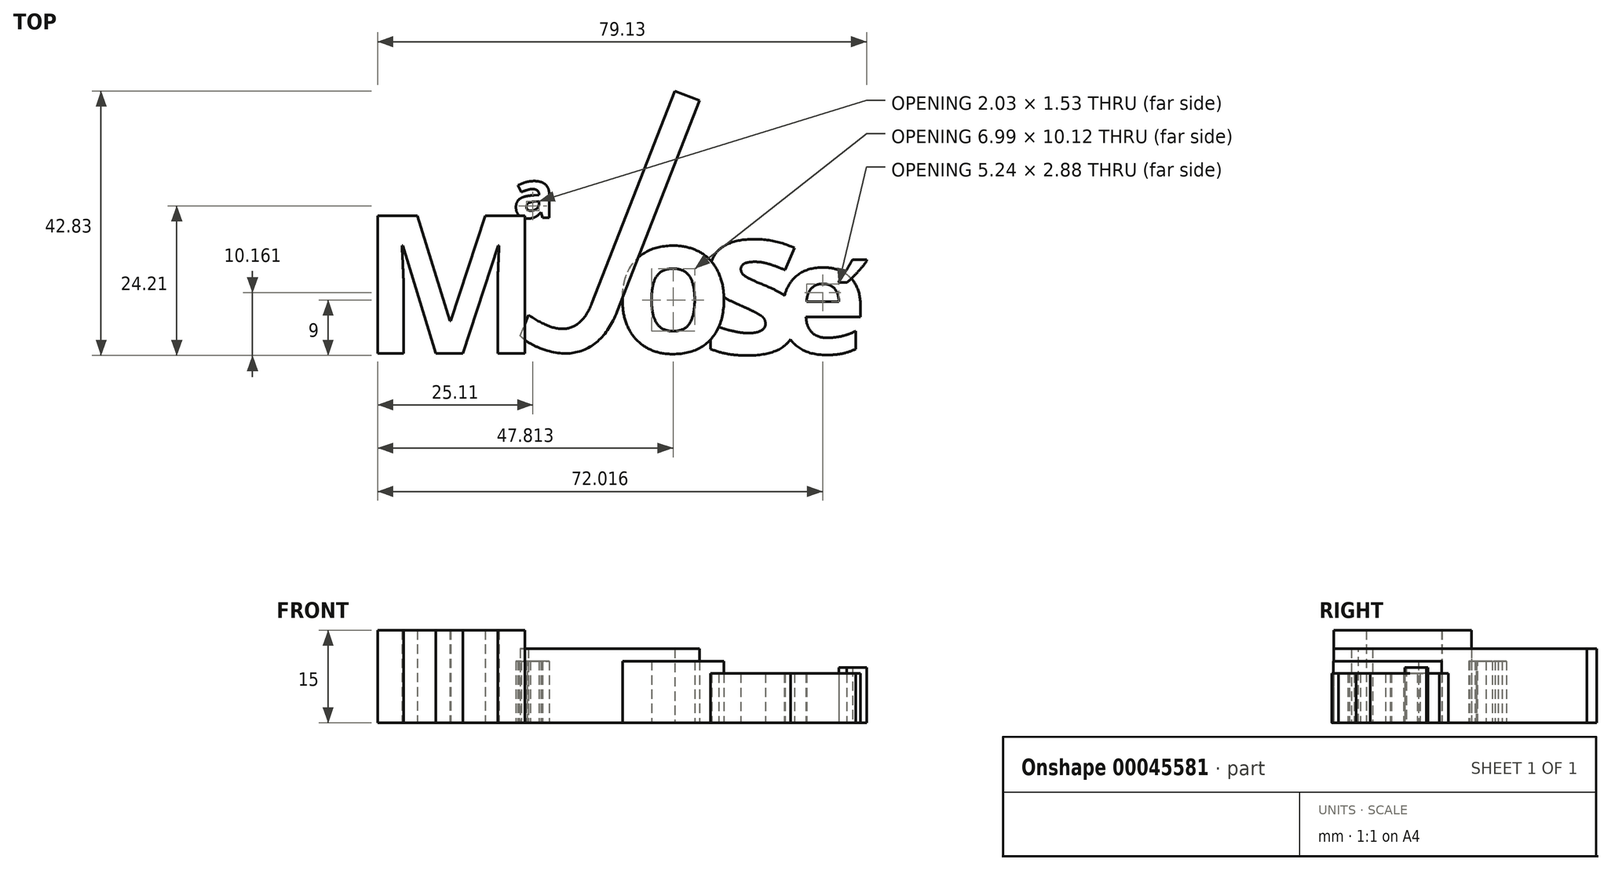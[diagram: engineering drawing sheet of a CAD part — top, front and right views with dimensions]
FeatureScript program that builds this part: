
annotation { "Feature Type Name" : "Feature", "Feature Type Description" : "" }
export const myFeature = defineFeature(function(context is Context, id is Id, definition is map)
    precondition{}
    {
        {
            var Q0;
            Q0=qCreatedBy(makeId("Top.planeOp"),FACE);
            var sketch = newSketch(context, id + "F0", { "sketchPlane" : qUnion([Q0])});
            skText(sketch, "E0", { "text": "M", "fontName": "OpenSans-Bold.ttf"});
            const initialGuessF0  = {"E0": [-0.0539, 0, 1, 0, 0.02249]};
            skSetInitialGuess(sketch, initialGuessF0);
            skSolve(sketch);
        }
        {
            var Q0;
            Q0=qCreatedBy(makeId("Top.planeOp"),FACE);
            var sketch = newSketch(context, id + "F1", { "sketchPlane" : qUnion([Q0])});
            skText(sketch, "E1", { "text": "ª", "fontName": "OpenSans-Bold.ttf"});
            const initialGuessF1  = {"E1": [-0.0291, 0.01558, 1, 0, 0.0123]};
            skSetInitialGuess(sketch, initialGuessF1);
            skSolve(sketch);
        }
        {
            var Q0;
            Q0=makeQuery(id+"F0.imprint","IMPRINT",FACE,{"disambiguationData":[TD([[makeQuery(id+"F0.imprint","IMPRINT",EDGE,{"derivedFrom":sQuery(id+"F0.wireOp",EDGE,"E0.sketch_text.stroke-0")}),-1.0]])]});
            extrude(context, id + "F2", {"entities" : qUnion([Q0]), "depth" : 15 * mm});
        }
        {
            var Q0;
            Q0 = qSketchRegion(id + "F1", true);
            extrude(context, id + "F3", {"entities" : qUnion([Q0]), "operationType" : NewBodyOperationType.ADD, "depth" : 10 * mm});
        }
        {
            var Q0;
            Q0=qCreatedBy(makeId("Top.planeOp"),FACE);
            var sketch = newSketch(context, id + "F4", { "sketchPlane" : qUnion([Q0])});
            skText(sketch, "E2", { "text": "J", "fontName": "OpenSans-Regular.ttf"});
            const initialGuessF4  = {"E2": [-0.02086, 0.00954, 1, 0, 0.0373]};
            skSetInitialGuess(sketch, initialGuessF4);
            skSolve(sketch);
        }
        {
            var Q0;
            Q0 = qSketchRegion(id + "F4", true);
            extrude(context, id + "F5", {"entities" : qUnion([Q0]), "depth" : 12 * mm});
        }
        {
            var Q0;
            Q0=qCreatedBy(makeId("Top.planeOp"),FACE);
            var sketch = newSketch(context, id + "F6", { "sketchPlane" : qUnion([Q0])});
            skText(sketch, "E3", { "text": "o", "fontName": "OpenSans-Bold.ttf"});
            const initialGuessF6  = {"E3": [-0.00896, 0.0002, 1, 0, 0.02234]};
            skSetInitialGuess(sketch, initialGuessF6);
            skSolve(sketch);
        }
        {
            var Q0;
            Q0=makeQuery(id+"F6.imprint","IMPRINT",FACE,{"disambiguationData":[TD([[makeQuery(id+"F6.imprint","IMPRINT",EDGE,{"derivedFrom":sQuery(id+"F6.wireOp",EDGE,"E3.sketch_text.stroke-0")}),-1.0]])]});
            extrude(context, id + "F7", {"entities" : qUnion([Q0]), "depth" : 10 * mm});
        }
        {
            var Q0;
            Q0=makeQuery(id+"F5.opExtrude","SWEPT_BODY",BODY,{"disambiguationData":[OSD([sQuery(id+"F4.wireOp",EDGE,"E2.sketch_text.stroke-0"),sQuery(id+"F4.wireOp",EDGE,"E2.sketch_text.stroke-1"),sQuery(id+"F4.wireOp",EDGE,"E2.sketch_text.stroke-2"),sQuery(id+"F4.wireOp",EDGE,"E2.sketch_text.stroke-3"),sQuery(id+"F4.wireOp",EDGE,"E2.sketch_text.stroke-4"),sQuery(id+"F4.wireOp",EDGE,"E2.sketch_text.stroke-5"),sQuery(id+"F4.wireOp",EDGE,"E2.sketch_text.stroke-6"),sQuery(id+"F4.wireOp",EDGE,"E2.sketch_text.stroke-7"),sQuery(id+"F4.wireOp",EDGE,"E2.sketch_text.stroke-8"),sQuery(id+"F4.wireOp",EDGE,"E2.sketch_text.stroke-9")])]});
            var Q1;
            Q1=makeQuery(id+"F5.opExtrude","SWEPT_EDGE",EDGE,{"disambiguationData":[OSD([sQuery(id+"F4.wireOp",EDGE,"E2.sketch_text.stroke-0"),sQuery(id+"F4.wireOp",EDGE,"E2.sketch_text.stroke-1")])]});
            transform(context, id + "F8", {"entities" : qUnion([Q0]), "transformType" : TransformType.ROTATION, "transformAxis" : qUnion([Q1]), "angle" : 21.35 * degree, "makeCopy" : false});
        }
        {
            var Q0;
            Q0=makeQuery(id+"F5.opExtrude","SWEPT_BODY",BODY,{"disambiguationData":[OSD([sQuery(id+"F4.wireOp",EDGE,"E2.sketch_text.stroke-0"),sQuery(id+"F4.wireOp",EDGE,"E2.sketch_text.stroke-1"),sQuery(id+"F4.wireOp",EDGE,"E2.sketch_text.stroke-2"),sQuery(id+"F4.wireOp",EDGE,"E2.sketch_text.stroke-3"),sQuery(id+"F4.wireOp",EDGE,"E2.sketch_text.stroke-4"),sQuery(id+"F4.wireOp",EDGE,"E2.sketch_text.stroke-5"),sQuery(id+"F4.wireOp",EDGE,"E2.sketch_text.stroke-6"),sQuery(id+"F4.wireOp",EDGE,"E2.sketch_text.stroke-7"),sQuery(id+"F4.wireOp",EDGE,"E2.sketch_text.stroke-8"),sQuery(id+"F4.wireOp",EDGE,"E2.sketch_text.stroke-9")])]});
            var Q1;
            Q1=makeQuery(id+"F2.opExtrude","CAP_EDGE",EDGE,{"disambiguationData":[OSD([sQuery(id+"F0.wireOp",EDGE,"E0.sketch_text.stroke-11")])],"isStart":false});
            var Q2;
            Q2=makeQuery(id+"F2.opExtrude","CAP_EDGE",EDGE,{"disambiguationData":[OSD([sQuery(id+"F0.wireOp",EDGE,"E0.sketch_text.stroke-11")])],"isStart":false});
            transform(context, id + "F9", {"entities" : qUnion([Q0]), "transformType" : TransformType.TRANSLATION_3D, "dx" : -3.09 * mm, "dy" : 2.36 * mm, "dz" : 0 * mm, "makeCopy" : false});
        }
        {
            var Q0;
            Q0=makeQuery(id+"F7.opExtrude","SWEPT_BODY",BODY,{"disambiguationData":[OSD([sQuery(id+"F6.wireOp",EDGE,"E3.sketch_text.stroke-0"),sQuery(id+"F6.wireOp",EDGE,"E3.sketch_text.stroke-1"),sQuery(id+"F6.wireOp",EDGE,"E3.sketch_text.stroke-2"),sQuery(id+"F6.wireOp",EDGE,"E3.sketch_text.stroke-3"),sQuery(id+"F6.wireOp",EDGE,"E3.sketch_text.stroke-4"),sQuery(id+"F6.wireOp",EDGE,"E3.sketch_text.stroke-5"),sQuery(id+"F6.wireOp",EDGE,"E3.sketch_text.stroke-6"),sQuery(id+"F6.wireOp",EDGE,"E3.sketch_text.stroke-7"),sQuery(id+"F6.wireOp",EDGE,"E3.sketch_text.stroke-8"),sQuery(id+"F6.wireOp",EDGE,"E3.sketch_text.stroke-9"),sQuery(id+"F6.wireOp",EDGE,"E3.sketch_text.stroke-10"),sQuery(id+"F6.wireOp",EDGE,"E3.sketch_text.stroke-11"),sQuery(id+"F6.wireOp",EDGE,"E3.sketch_text.stroke-12"),sQuery(id+"F6.wireOp",EDGE,"E3.sketch_text.stroke-13"),sQuery(id+"F6.wireOp",EDGE,"E3.sketch_text.stroke-14"),sQuery(id+"F6.wireOp",EDGE,"E3.sketch_text.stroke-15"),sQuery(id+"F6.wireOp",EDGE,"E3.sketch_text.stroke-16"),sQuery(id+"F6.wireOp",EDGE,"E3.sketch_text.stroke-17")])]});
            transform(context, id + "F10", {"entities" : qUnion([Q0]), "transformType" : TransformType.TRANSLATION_3D, "dx" : -3.91 * mm, "dy" : 0 * mm, "dz" : 0 * mm, "makeCopy" : false});
        }
        {
            var Q0;
            Q0=qCreatedBy(makeId("Top.planeOp"),FACE);
            var sketch = newSketch(context, id + "F11", { "sketchPlane" : qUnion([Q0])});
            skText(sketch, "E4", { "text": "s", "fontName": "OpenSans-Bold.ttf"});
            const initialGuessF11  = {"E4": [0.00127, 0, 1, 0, 0.02397]};
            skSetInitialGuess(sketch, initialGuessF11);
            skSolve(sketch);
        }
        {
            var Q0;
            Q0 = qSketchRegion(id + "F11", true);
            extrude(context, id + "F12", {"entities" : qUnion([Q0]), "operationType" : NewBodyOperationType.ADD, "depth" : 8 * mm});
        }
        {
            var Q0;
            Q0=qCreatedBy(makeId("Top.planeOp"),FACE);
            var sketch = newSketch(context, id + "F13", { "sketchPlane" : qUnion([Q0])});
            skText(sketch, "E5", { "text": "e", "fontName": "OpenSans-Bold.ttf"});
            const initialGuessF13  = {"E5": [0.01332, 0, 1, 0, 0.01803]};
            skSetInitialGuess(sketch, initialGuessF13);
            skSolve(sketch);
        }
        {
            var Q0;
            Q0 = qSketchRegion(id + "F13", true);
            extrude(context, id + "F14", {"entities" : qUnion([Q0]), "operationType" : NewBodyOperationType.ADD, "depth" : 8 * mm});
        }
        {
            var Q0;
            Q0=qCreatedBy(makeId("Top.planeOp"),FACE);
            var sketch = newSketch(context, id + "F15", { "sketchPlane" : qUnion([Q0])});
            skText(sketch, "E6", { "text": "´", "fontName": "OpenSans-Regular.ttf"});
            const initialGuessF15  = {"E6": [0.02767, 0.0147, 1, 0, 0.01682]};
            skSetInitialGuess(sketch, initialGuessF15);
            skSolve(sketch);
        }
        {
            var Q0;
            Q0 = qSketchRegion(id + "F15", true);
            extrude(context, id + "F16", {"entities" : qUnion([Q0]), "depth" : 9 * mm});
        }
        {
            var Q0;
            Q0=makeQuery(id+"F16.opExtrude","SWEPT_BODY",BODY,{"disambiguationData":[OSD([sQuery(id+"F15.wireOp",EDGE,"E6.sketch_text.stroke-0"),sQuery(id+"F15.wireOp",EDGE,"E6.sketch_text.stroke-1"),sQuery(id+"F15.wireOp",EDGE,"E6.sketch_text.stroke-2"),sQuery(id+"F15.wireOp",EDGE,"E6.sketch_text.stroke-3"),sQuery(id+"F15.wireOp",EDGE,"E6.sketch_text.stroke-4"),sQuery(id+"F15.wireOp",EDGE,"E6.sketch_text.stroke-5"),sQuery(id+"F15.wireOp",EDGE,"E6.sketch_text.stroke-6"),sQuery(id+"F15.wireOp",EDGE,"E6.sketch_text.stroke-7")])]});
            transform(context, id + "F17", {"entities" : qUnion([Q0]), "transformType" : TransformType.TRANSLATION_3D, "dx" : -8.6 * mm, "dy" : -17.4 * mm, "dz" : 0 * mm, "makeCopy" : false});
        }
    });
